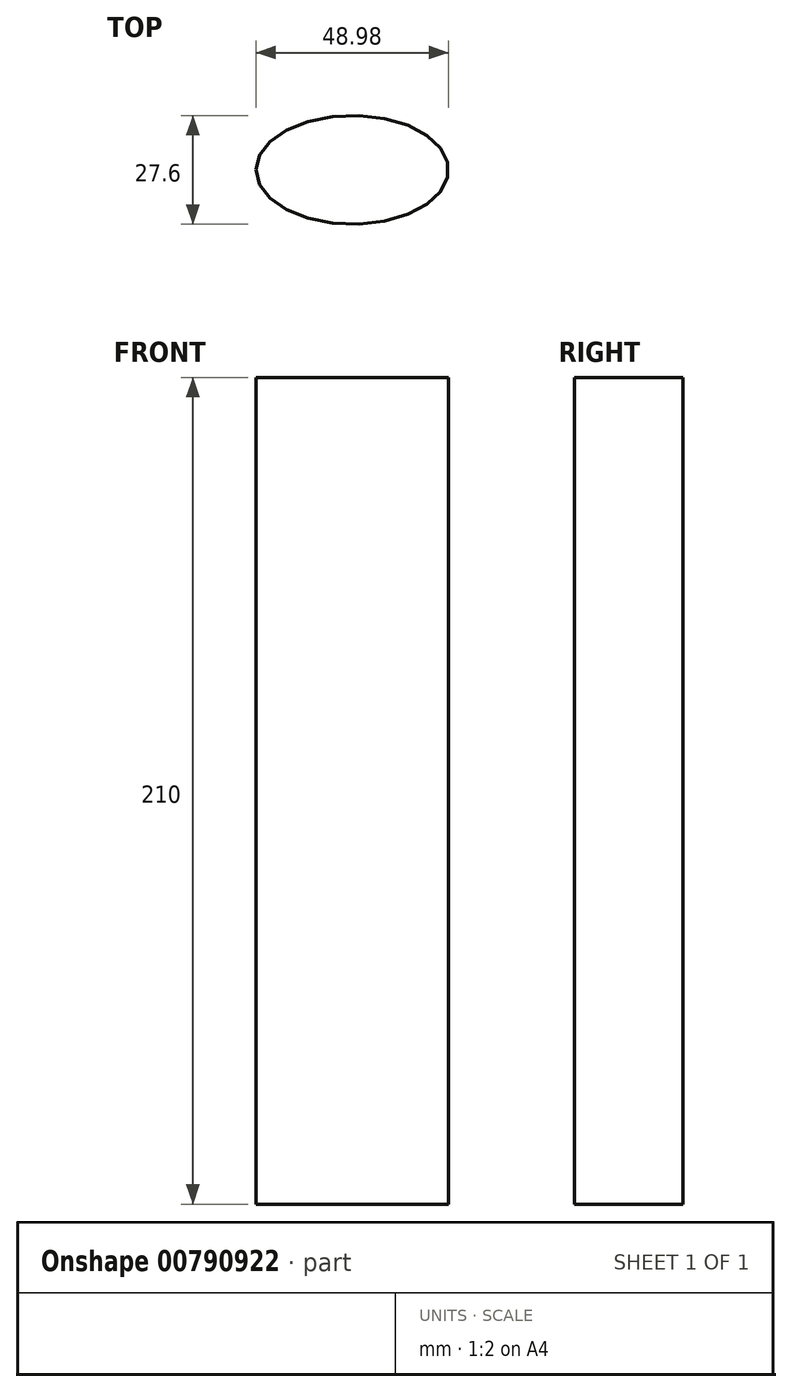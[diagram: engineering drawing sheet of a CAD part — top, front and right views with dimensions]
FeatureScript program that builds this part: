
annotation { "Feature Type Name" : "Feature", "Feature Type Description" : "" }
export const myFeature = defineFeature(function(context is Context, id is Id, definition is map)
    precondition{}
    {
        {
            var Q0;
            Q0=qCreatedBy(makeId("Top.planeOp"),FACE);
            var sketch = newSketch(context, id + "F0", { "sketchPlane" : qUnion([Q0])});
            skEllipse(sketch, "E0", {"center": v(0, 0) * mm, "majorRadius": 24.49 * mm, "minorRadius": 13.8 * mm, "majorAxis": v(-1, 0)});
            skSolve(sketch);
        }
        {
            var Q0;
            Q0=sQuery(id+"F0.wireOp",EDGE,"E0");
            extrude(context, id + "F1", {"bodyType" : ToolBodyType.SURFACE, "surfaceEntities" : qUnion([Q0]), "depth" : 210 * mm, "offsetDistance" : 25 * mm});
        }
    });
